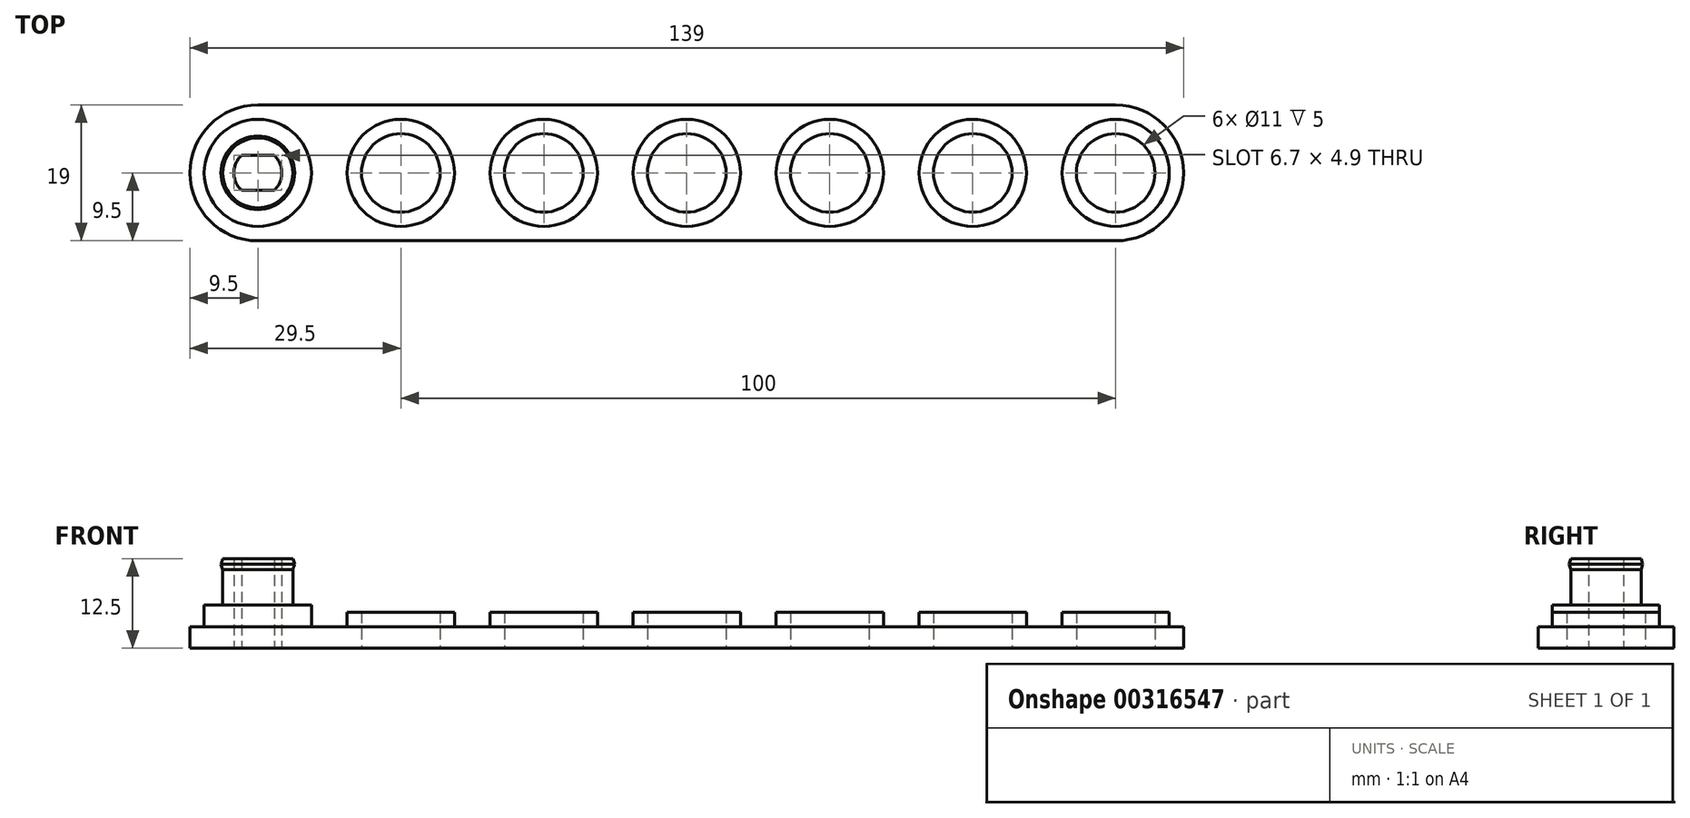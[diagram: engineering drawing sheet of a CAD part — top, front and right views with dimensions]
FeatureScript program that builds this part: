
annotation { "Feature Type Name" : "Feature", "Feature Type Description" : "" }
export const myFeature = defineFeature(function(context is Context, id is Id, definition is map)
    precondition{}
    {
        {
            assignVariable(context, id + "F0", {"name" : "e", "anyValue" : 3});
        }
        {
            assignVariable(context, id + "F1", {"name" : "h0", "anyValue" : 2});
        }
        {
            var Q0;
            Q0=qCreatedBy(makeId("Top.planeOp"),FACE);
            var sketch = newSketch(context, id + "F2", { "sketchPlane" : qUnion([Q0])});
            skLineSegment(sketch, "E0.bottom", {"start": v(20, 9.5) * mm, "end": v(140, 9.5) * mm});
            skLineSegment(sketch, "E0.top", {"start": v(20, -9.5) * mm, "end": v(140, -9.5) * mm});
            skLineSegment(sketch, "E0.left", {"start": v(-9.5, 0) * mm, "end": v(-9.5, 0) * mm});
            skLineSegment(sketch, "E0.right", {"start": v(149.5, 0) * mm, "end": v(149.5, 0) * mm});
            skPoint(sketch, "E1", {"position": v(-9.5, 0) * mm});
            skPoint(sketch, "E2.visualSharp", {"position": v(149.5, 9.5) * mm});
            skArc(sketch, "E2.filletArc", {"start": v(149.5, 0) * mm, "mid": v(146.72, 6.72) * mm, "end": v(140, 9.5) * mm});
            skPoint(sketch, "E3.visualSharp", {"position": v(149.5, -9.5) * mm});
            skArc(sketch, "E3.filletArc", {"start": v(140, -9.5) * mm, "mid": v(146.72, -6.72) * mm, "end": v(149.5, 0) * mm});
            skPoint(sketch, "E4.visualSharp", {"position": v(-9.5, -9.5) * mm});
            skPoint(sketch, "E5.visualSharp", {"position": v(-9.5, 9.5) * mm});
            skCircle(sketch, "E6.1.0.0", {"center": v(20, 0) * mm, "radius": 5.5 * mm});
            skCircle(sketch, "E6.1.0.1", {"center": v(20, 0) * mm, "radius": 7.5 * mm});
            skCircle(sketch, "E6.2.0.0", {"center": v(40, 0) * mm, "radius": 5.5 * mm});
            skCircle(sketch, "E6.2.0.1", {"center": v(40, 0) * mm, "radius": 7.5 * mm});
            skCircle(sketch, "E7.0.3.0", {"center": v(60, 0) * mm, "radius": 5.5 * mm});
            skCircle(sketch, "E7.2.3.0", {"center": v(60, 0) * mm, "radius": 7.5 * mm});
            skCircle(sketch, "E7.0.4.0", {"center": v(80, 0) * mm, "radius": 5.5 * mm});
            skCircle(sketch, "E7.2.4.0", {"center": v(80, 0) * mm, "radius": 7.5 * mm});
            skCircle(sketch, "E7.0.5.0", {"center": v(100, 0) * mm, "radius": 5.5 * mm});
            skCircle(sketch, "E7.2.5.0", {"center": v(100, 0) * mm, "radius": 7.5 * mm});
            skCircle(sketch, "E7.0.6.0", {"center": v(120, 0) * mm, "radius": 5.5 * mm});
            skCircle(sketch, "E7.2.6.0", {"center": v(120, 0) * mm, "radius": 7.5 * mm});
            skCircle(sketch, "E7.0.7.0", {"center": v(140, 0) * mm, "radius": 5.5 * mm});
            skCircle(sketch, "E7.2.7.0", {"center": v(140, 0) * mm, "radius": 7.5 * mm});
            skPoint(sketch, "E8", {"position": v(20, 9.5) * mm});
            skPoint(sketch, "E9", {"position": v(20, -9.5) * mm});
            skArc(sketch, "E10", {"start": v(20, 9.5) * mm, "mid": v(10.5, 0) * mm, "end": v(20, -9.5) * mm});
            skPoint(sketch, "E11.orphan", {"position": v(0, 0) * mm});
            skLineSegment(sketch, "E12", {"start": v(20, 0) * mm, "end": v(20, -2.45) * mm, "construction": true});
            skLineSegment(sketch, "E13", {"start": v(20, 0) * mm, "end": v(20, 2.45) * mm, "construction": true});
            skCircle(sketch, "E14", {"center": v(20, 0) * mm, "radius": 3.35 * mm, "construction": true});
            skLineSegment(sketch, "E15", {"start": v(20, -2.45) * mm, "end": v(17.72, -2.45) * mm});
            skLineSegment(sketch, "E16", {"start": v(20, -2.45) * mm, "end": v(22.28, -2.45) * mm});
            skLineSegment(sketch, "E17", {"start": v(20, 2.45) * mm, "end": v(22.28, 2.45) * mm});
            skLineSegment(sketch, "E18", {"start": v(20, 2.45) * mm, "end": v(17.72, 2.45) * mm});
            skArc(sketch, "E19", {"start": v(17.72, -2.45) * mm, "mid": v(16.65, 0) * mm, "end": v(17.72, 2.45) * mm});
            skArc(sketch, "E20", {"start": v(22.28, -2.45) * mm, "mid": v(23.35, 0) * mm, "end": v(22.28, 2.45) * mm});
            skCircle(sketch, "E21", {"center": v(20, 0) * mm, "radius": 4.9 * mm});
            skSolve(sketch);
        }
        {
            var Q0;
            Q0=qSketchRegion(id+"F2",true);
            var Q1;
            Q1=makeQuery(id+"F2.imprint","IMPRINT",FACE,{"disambiguationData":[TD([[makeQuery(id+"F2.imprint","IMPRINT",EDGE,{"derivedFrom":sQuery(id+"F2.wireOp",EDGE,"Sm7aKCzd-n855-EbMJ-dOnY-vjKQaanzyYti")}),-1.0]])]});
            var Q2;
            Q2=makeQuery(id+"F2.imprint","IMPRINT",FACE,{"disambiguationData":[TD([[makeQuery(id+"F2.imprint","IMPRINT",EDGE,{"derivedFrom":sQuery(id+"F2.wireOp",EDGE,"E6.1.0.0")}),-1.0]])]});
            var Q3;
            Q3=makeQuery(id+"F2.imprint","IMPRINT",FACE,{"disambiguationData":[TD([[makeQuery(id+"F2.imprint","IMPRINT",EDGE,{"derivedFrom":sQuery(id+"F2.wireOp",EDGE,"E6.2.0.0")}),-1.0]])]});
            var Q4;
            Q4=makeQuery(id+"F2.imprint","IMPRINT",FACE,{"disambiguationData":[TD([[makeQuery(id+"F2.imprint","IMPRINT",EDGE,{"derivedFrom":sQuery(id+"F2.wireOp",EDGE,"345b2114-0edb-480d-a68f-e22b198684d9.0.3.0")}),-1.0]])]});
            var Q5;
            Q5=makeQuery(id+"F2.imprint","IMPRINT",FACE,{"disambiguationData":[TD([[makeQuery(id+"F2.imprint","IMPRINT",EDGE,{"derivedFrom":sQuery(id+"F2.wireOp",EDGE,"E7.0.3.0")}),-1.0]])]});
            var Q6;
            Q6=makeQuery(id+"F2.imprint","IMPRINT",FACE,{"disambiguationData":[TD([[makeQuery(id+"F2.imprint","IMPRINT",EDGE,{"derivedFrom":sQuery(id+"F2.wireOp",EDGE,"E7.0.4.0")}),-1.0]])]});
            var Q7;
            Q7=makeQuery(id+"F2.imprint","IMPRINT",FACE,{"disambiguationData":[TD([[makeQuery(id+"F2.imprint","IMPRINT",EDGE,{"derivedFrom":sQuery(id+"F2.wireOp",EDGE,"E7.0.5.0")}),-1.0]])]});
            var Q8;
            Q8=makeQuery(id+"F2.imprint","IMPRINT",FACE,{"disambiguationData":[TD([[makeQuery(id+"F2.imprint","IMPRINT",EDGE,{"derivedFrom":sQuery(id+"F2.wireOp",EDGE,"E7.0.6.0")}),-1.0]])]});
            var Q9;
            Q9=makeQuery(id+"F2.imprint","IMPRINT",FACE,{"disambiguationData":[TD([[makeQuery(id+"F2.imprint","IMPRINT",EDGE,{"derivedFrom":sQuery(id+"F2.wireOp",EDGE,"E7.0.7.0")}),-1.0]])]});
            var Q10;
            Q10=makeQuery(id+"F2.imprint","IMPRINT",FACE,{"disambiguationData":[TD([[makeQuery(id+"F2.imprint","IMPRINT",EDGE,{"derivedFrom":sQuery(id+"F2.wireOp",EDGE,"eb742b51-7e77-48c1-a0eb-fe54fb8ff7c7.0.8.0")}),-1.0]])]});
            var Q11;
            Q11=makeQuery(id+"F2.imprint","IMPRINT",FACE,{"disambiguationData":[TD([[makeQuery(id+"F2.imprint","IMPRINT",EDGE,{"derivedFrom":sQuery(id+"F2.wireOp",EDGE,"eb742b51-7e77-48c1-a0eb-fe54fb8ff7c7.0.9.0")}),-1.0]])]});
            extrude(context, id + "F3", {"entities" : qUnion([Q0, Q1, Q2, Q3, Q4, Q5, Q6, Q7, Q8, Q9, Q10, Q11]), "depth" : (getVariable(context, 'e')) * mm});
        }
        {
            var Q0;
            Q0=makeQuery(id+"F2.imprint","IMPRINT",FACE,{"disambiguationData":[TD([[makeQuery(id+"F2.imprint","IMPRINT",EDGE,{"derivedFrom":sQuery(id+"F2.wireOp",EDGE,"Sm7aKCzd-n855-EbMJ-dOnY-vjKQaanzyYti")}),-1.0]])]});
            var Q1;
            Q1=makeQuery(id+"F2.imprint","IMPRINT",FACE,{"disambiguationData":[TD([[makeQuery(id+"F2.imprint","IMPRINT",EDGE,{"derivedFrom":sQuery(id+"F2.wireOp",EDGE,"E6.1.0.0")}),-1.0]])]});
            var Q2;
            Q2=makeQuery(id+"F2.imprint","IMPRINT",FACE,{"disambiguationData":[TD([[makeQuery(id+"F2.imprint","IMPRINT",EDGE,{"derivedFrom":sQuery(id+"F2.wireOp",EDGE,"E6.2.0.0")}),-1.0]])]});
            var Q3;
            Q3=makeQuery(id+"F2.imprint","IMPRINT",FACE,{"disambiguationData":[TD([[makeQuery(id+"F2.imprint","IMPRINT",EDGE,{"derivedFrom":sQuery(id+"F2.wireOp",EDGE,"345b2114-0edb-480d-a68f-e22b198684d9.0.3.0")}),-1.0]])]});
            var Q4;
            Q4=makeQuery(id+"F2.imprint","IMPRINT",FACE,{"disambiguationData":[TD([[makeQuery(id+"F2.imprint","IMPRINT",EDGE,{"derivedFrom":sQuery(id+"F2.wireOp",EDGE,"E7.0.3.0")}),-1.0]])]});
            var Q5;
            Q5=makeQuery(id+"F2.imprint","IMPRINT",FACE,{"disambiguationData":[TD([[makeQuery(id+"F2.imprint","IMPRINT",EDGE,{"derivedFrom":sQuery(id+"F2.wireOp",EDGE,"E7.0.4.0")}),-1.0]])]});
            var Q6;
            Q6=makeQuery(id+"F2.imprint","IMPRINT",FACE,{"disambiguationData":[TD([[makeQuery(id+"F2.imprint","IMPRINT",EDGE,{"derivedFrom":sQuery(id+"F2.wireOp",EDGE,"E7.0.5.0")}),-1.0]])]});
            var Q7;
            Q7=makeQuery(id+"F2.imprint","IMPRINT",FACE,{"disambiguationData":[TD([[makeQuery(id+"F2.imprint","IMPRINT",EDGE,{"derivedFrom":sQuery(id+"F2.wireOp",EDGE,"E7.0.6.0")}),-1.0]])]});
            var Q8;
            Q8=makeQuery(id+"F2.imprint","IMPRINT",FACE,{"disambiguationData":[TD([[makeQuery(id+"F2.imprint","IMPRINT",EDGE,{"derivedFrom":sQuery(id+"F2.wireOp",EDGE,"E7.0.7.0")}),-1.0]])]});
            var Q9;
            Q9=makeQuery(id+"F2.imprint","IMPRINT",FACE,{"disambiguationData":[TD([[makeQuery(id+"F2.imprint","IMPRINT",EDGE,{"derivedFrom":sQuery(id+"F2.wireOp",EDGE,"eb742b51-7e77-48c1-a0eb-fe54fb8ff7c7.0.8.0")}),-1.0]])]});
            var Q10;
            Q10=makeQuery(id+"F2.imprint","IMPRINT",FACE,{"disambiguationData":[TD([[makeQuery(id+"F2.imprint","IMPRINT",EDGE,{"derivedFrom":sQuery(id+"F2.wireOp",EDGE,"eb742b51-7e77-48c1-a0eb-fe54fb8ff7c7.0.9.0")}),-1.0]])]});
            extrude(context, id + "F4", {"entities" : qUnion([Q0, Q1, Q2, Q3, Q4, Q5, Q6, Q7, Q8, Q9, Q10]), "operationType" : NewBodyOperationType.ADD, "depth" : (getVariable(context, 'e') + getVariable(context, 'h0')) * mm});
        }
        {
            var Q0;
            Q0=makeQuery(id+"F2.imprint","IMPRINT",FACE,{"disambiguationData":[TD([[makeQuery(id+"F2.imprint","IMPRINT",EDGE,{"derivedFrom":sQuery(id+"F2.wireOp",EDGE,"c60a1688-5068-4c90-a7dd-35f8f5ad3e8d")}),-1.0]])]});
            var Q1;
            Q1=makeQuery(id+"F2.imprint","IMPRINT",FACE,{"disambiguationData":[TD([[makeQuery(id+"F2.imprint","IMPRINT",EDGE,{"derivedFrom":sQuery(id+"F2.wireOp",EDGE,"7b80f376-3599-4fde-ab00-e33546d4e86b")}),1.0]])]});
            var Q2;
            Q2=makeQuery(id+"F2.imprint","IMPRINT",FACE,{"disambiguationData":[TD([[makeQuery(id+"F2.imprint","IMPRINT",EDGE,{"derivedFrom":sQuery(id+"F2.wireOp",EDGE,"E7.2.7.0")}),1.0]])]});
            extrude(context, id + "F5", {"entities" : qUnion([Q0, Q1, Q2]), "operationType" : NewBodyOperationType.ADD, "depth" : 5 * mm});
        }
        {
            var Q0;
            Q0=makeQuery(id+"F2.imprint","IMPRINT",FACE,{"disambiguationData":[TD([[makeQuery(id+"F2.imprint","IMPRINT",EDGE,{"derivedFrom":sQuery(id+"F2.wireOp",EDGE,"E6.1.0.0")}),1.0]])]});
            var Q1;
            Q1=makeQuery(id+"F2.imprint","IMPRINT",FACE,{"disambiguationData":[TD([[makeQuery(id+"F2.imprint","IMPRINT",EDGE,{"derivedFrom":sQuery(id+"F2.wireOp",EDGE,"E6.1.0.0")}),-1.0]])]});
            extrude(context, id + "F6", {"entities" : qUnion([Q0, Q1]), "operationType" : NewBodyOperationType.ADD, "depth" : 6 * mm});
        }
        {
            var Q0;
            Q0=makeQuery(id+"F2.imprint","IMPRINT",FACE,{"disambiguationData":[TD([[makeQuery(id+"F2.imprint","IMPRINT",EDGE,{"derivedFrom":sQuery(id+"F2.wireOp",EDGE,"E15")}),1.0]])]});
            extrude(context, id + "F7", {"entities" : qUnion([Q0]), "operationType" : NewBodyOperationType.ADD, "depth" : 12.5 * mm});
        }
        {
            var Q0;
            Q0=makeQuery(id+"F7.opExtrude","SWEPT_FACE",FACE,{"disambiguationData":[OSD([sQuery(id+"F2.wireOp",EDGE,"E17"),sQuery(id+"F2.wireOp",EDGE,"E18")])]});
            var Q1;
            Q1=sQuery(id+"F2.wireOp",VERTEX,"E21.center");
            cPlane(context, id + "F8", {"entities" : qUnion([Q0, Q1]), "cplaneType" : CPlaneType.PLANE_POINT, "offset" : 25 * mm, "width" : 150 * mm, "height" : 150 * mm});
        }
        {
            var Q0;
            Q0=qCreatedBy(id+"F8.planeOp",FACE);
            var sketch = newSketch(context, id + "F9", { "sketchPlane" : qUnion([Q0])});
            skPoint(sketch, "E22.0", {"position": v(20, 0) * mm});
            skLineSegment(sketch, "E23.0", {"start": v(15.1, 12.5) * mm, "end": v(24.9, 12.5) * mm});
            skLineSegment(sketch, "E24", {"start": v(20, 0) * mm, "end": v(20, 12.5) * mm});
            skLineSegment(sketch, "E25", {"start": v(24.9, 12.5) * mm, "end": v(24.9, 11) * mm});
            skPoint(sketch, "E26", {"position": v(24.9, 11.75) * mm});
            skLineSegment(sketch, "E27", {"start": v(24.9, 11.75) * mm, "end": v(25.15, 11.75) * mm, "construction": true});
            skLineSegment(sketch, "E28", {"start": v(25.15, 11.75) * mm, "end": v(24.9, 12.5) * mm});
            skLineSegment(sketch, "E29", {"start": v(25.15, 11.75) * mm, "end": v(24.9, 11) * mm});
            skSolve(sketch);
        }
        {
            var Q0;
            Q0=makeQuery(id+"F9.imprint","IMPRINT",FACE,{"disambiguationData":[TD([[makeQuery(id+"F9.imprint","IMPRINT",EDGE,{"derivedFrom":sQuery(id+"F9.wireOp",EDGE,"E25")}),1.0]])]});
            var Q1;
            Q1=sQuery(id+"F9.wireOp",EDGE,"E24");
            revolve(context, id + "F10", {"operationType" : NewBodyOperationType.ADD, "entities" : qUnion([Q0]), "axis" : qUnion([Q1]), "revolveType" : RevolveType.FULL});
        }
    });
